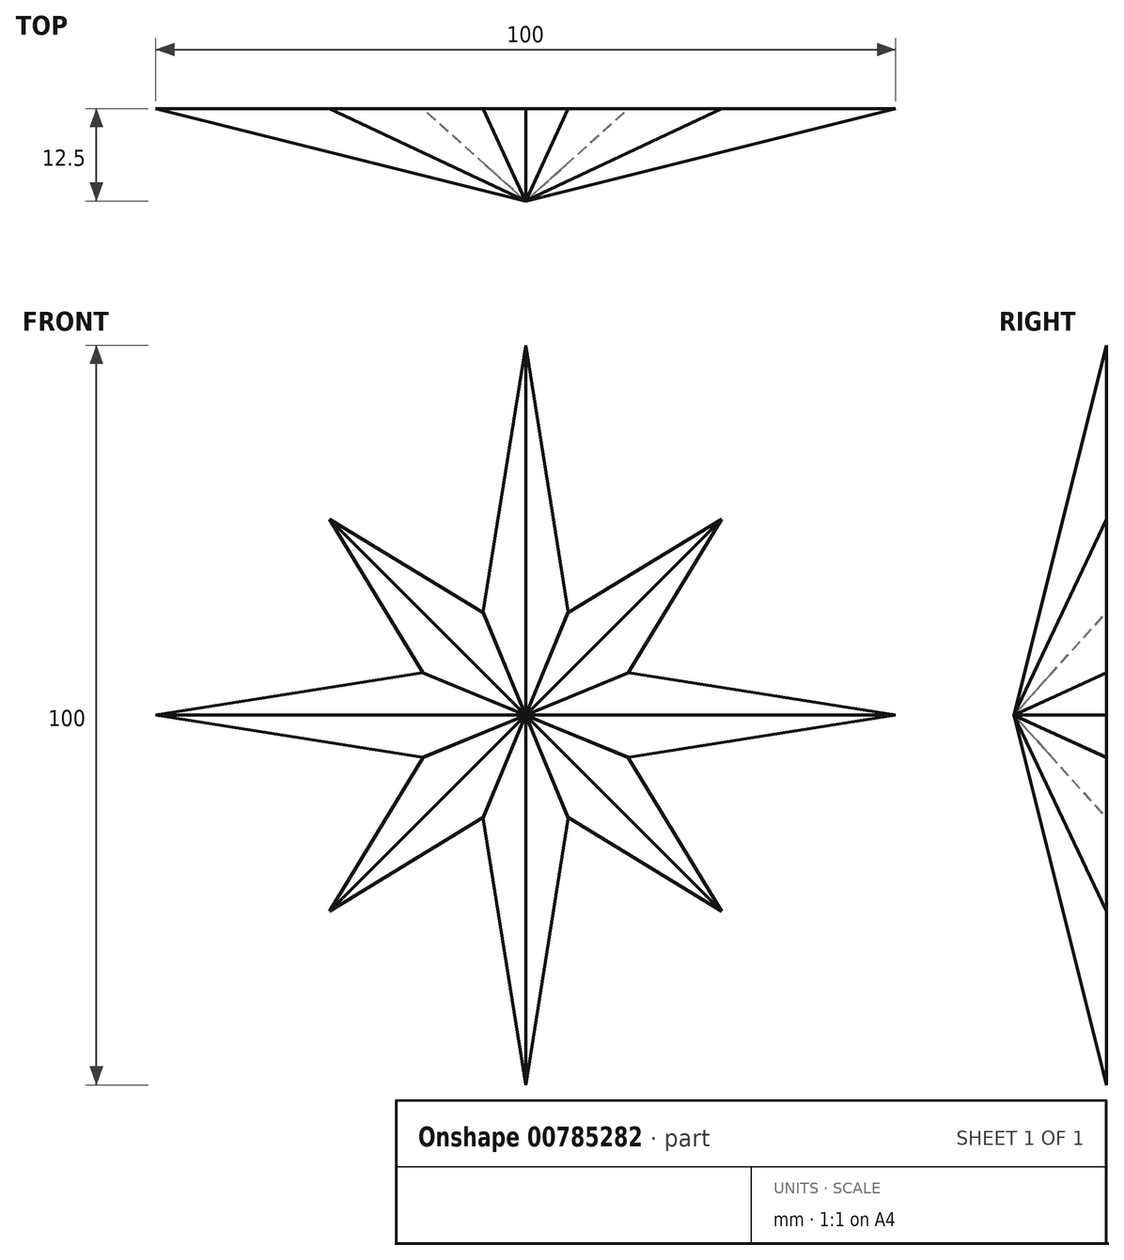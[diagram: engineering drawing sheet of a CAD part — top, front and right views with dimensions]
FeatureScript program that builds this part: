
annotation { "Feature Type Name" : "Feature", "Feature Type Description" : "" }
export const myFeature = defineFeature(function(context is Context, id is Id, definition is map)
    precondition{}
    {
        {
            var Q0;
            Q0=qCreatedBy(makeId("Front.planeOp"),FACE);
            var sketch = newSketch(context, id + "F0", { "sketchPlane" : qUnion([Q0])});
            skLineSegment(sketch, "E0", {"start": v(0, 0) * mm, "end": v(-50, 0) * mm});
            skLineSegment(sketch, "E1", {"start": v(0, 0) * mm, "end": v(-26.52, 26.52) * mm});
            skLineSegment(sketch, "E2", {"start": v(0, 0) * mm, "end": v(-13.86, 5.74) * mm});
            skPoint(sketch, "E3.center", {"position": v(0, 0) * mm});
            skLineSegment(sketch, "E4", {"start": v(-50, 0) * mm, "end": v(-13.86, 5.74) * mm});
            skLineSegment(sketch, "E5", {"start": v(-13.86, 5.74) * mm, "end": v(-26.52, 26.52) * mm});
            skSolve(sketch);
        }
        {
            var Q0;
            Q0=qCreatedBy(makeId("Right.planeOp"),FACE);
            var sketch = newSketch(context, id + "F1", { "sketchPlane" : qUnion([Q0])});
            skLineSegment(sketch, "E6", {"start": v(0, 0) * mm, "end": v(-12.5, 0) * mm});
            skSolve(sketch);
        }
        {
            var Q0;
            Q0=makeQuery(id+"F0.imprint","IMPRINT",FACE,{"disambiguationData":[TD([[makeQuery(id+"F0.imprint","IMPRINT",EDGE,{"derivedFrom":sQuery(id+"F0.wireOp",EDGE,"E0")}),-1.0]])]});
            var Q1;
            Q1=makeQuery(id+"F0.imprint","IMPRINT",FACE,{"disambiguationData":[TD([[makeQuery(id+"F0.imprint","IMPRINT",EDGE,{"derivedFrom":sQuery(id+"F0.wireOp",EDGE,"E1")}),1.0]])]});
            var Q2;
            Q2=sQuery(id+"F1.wireOp",VERTEX,"E6.end");
            extrude(context, id + "F2", {"entities" : qUnion([Q0, Q1]), "endBound" : BoundingType.UP_TO_VERTEX, "depth" : 25 * mm, "endBoundEntityVertex" : qUnion([Q2]), "offsetDistance" : 25 * mm});
        }
        {
            var Q0;
            Q0=sQuery(id+"F1.wireOp",VERTEX,"E6.end");
            var Q1;
            Q1=sQuery(id+"F0.wireOp",VERTEX,"E2.end");
            var Q2;
            Q2=sQuery(id+"F0.wireOp",VERTEX,"E0.end");
            cPlane(context, id + "F3", {"entities" : qUnion([Q0, Q1, Q2]), "cplaneType" : CPlaneType.THREE_POINT, "offset" : 25 * mm, "width" : 150 * mm, "height" : 150 * mm});
        }
        {
            var Q0;
            Q0=qCreatedBy(id+"F3.planeOp",FACE);
            var sketch = newSketch(context, id + "F4", { "sketchPlane" : qUnion([Q0])});
            skLineSegment(sketch, "E7", {"start": v(-53.08, -2.38) * mm, "end": v(-48.34, 21) * mm});
            skLineSegment(sketch, "E8", {"start": v(-48.34, 21) * mm, "end": v(0.9, 10.55) * mm});
            skLineSegment(sketch, "E9", {"start": v(0.9, 10.55) * mm, "end": v(-44.29, -33.47) * mm});
            skLineSegment(sketch, "E10", {"start": v(-44.29, -33.47) * mm, "end": v(-53.08, -2.38) * mm});
            skSolve(sketch);
        }
        {
            var Q0;
            Q0=makeQuery(id+"F4.imprint","IMPRINT",FACE,{"disambiguationData":[TD([[makeQuery(id+"F4.imprint","IMPRINT",EDGE,{"derivedFrom":sQuery(id+"F4.wireOp",EDGE,"E7")}),-1.0]])]});
            extrude(context, id + "F5", {"entities" : qUnion([Q0]), "depth" : -50 * mm, "offsetDistance" : 25 * mm});
        }
        {
            var Q0;
            Q0=makeQuery(id+"F5.opExtrude","SWEPT_BODY",BODY,{"disambiguationData":[OSD([sQuery(id+"F4.wireOp",EDGE,"E7"),sQuery(id+"F4.wireOp",EDGE,"E8"),sQuery(id+"F4.wireOp",EDGE,"E9"),sQuery(id+"F4.wireOp",EDGE,"E10")])]});
            var Q1;
            Q1=makeQuery(id+"F2.opExtrude","SWEPT_BODY",BODY,{"disambiguationData":[OSD([sQuery(id+"F0.wireOp",EDGE,"E0"),sQuery(id+"F0.wireOp",EDGE,"E1"),sQuery(id+"F0.wireOp",EDGE,"E4"),sQuery(id+"F0.wireOp",EDGE,"E5")])]});
            booleanBodies(context, id + "F6", {"operationType" : BooleanOperationType.SUBTRACTION, "tools" : qUnion([Q0]), "targets" : qUnion([Q1])});
        }
        {
            var Q0;
            Q0=sQuery(id+"F0.wireOp",VERTEX,"E2.end");
            var Q1;
            Q1=sQuery(id+"F1.wireOp",VERTEX,"E6.end");
            var Q2;
            Q2=sQuery(id+"F0.wireOp",VERTEX,"E1.end");
            cPlane(context, id + "F7", {"entities" : qUnion([Q0, Q1, Q2]), "cplaneType" : CPlaneType.THREE_POINT, "offset" : 25 * mm, "width" : 150 * mm, "height" : 150 * mm});
        }
        {
            var Q0;
            Q0=qCreatedBy(id+"F7.planeOp",FACE);
            var sketch = newSketch(context, id + "F8", { "sketchPlane" : qUnion([Q0])});
            skLineSegment(sketch, "E11", {"start": v(-10.2, 0) * mm, "end": v(5.37, 12.32) * mm});
            skLineSegment(sketch, "E12", {"start": v(5.37, 12.32) * mm, "end": v(8.1, 37.54) * mm});
            skLineSegment(sketch, "E13", {"start": v(8.1, 37.54) * mm, "end": v(-11, 36.94) * mm});
            skLineSegment(sketch, "E14", {"start": v(-11, 36.94) * mm, "end": v(-10.2, 0) * mm});
            skSolve(sketch);
        }
        {
            var Q0;
            Q0=makeQuery(id+"F8.imprint","IMPRINT",FACE,{"disambiguationData":[TD([[makeQuery(id+"F8.imprint","IMPRINT",EDGE,{"derivedFrom":sQuery(id+"F8.wireOp",EDGE,"E11")}),1.0]])]});
            extrude(context, id + "F9", {"entities" : qUnion([Q0]), "depth" : -50 * mm, "offsetDistance" : 25 * mm});
        }
        {
            var Q0;
            Q0=makeQuery(id+"F9.opExtrude","SWEPT_BODY",BODY,{"disambiguationData":[OSD([sQuery(id+"F8.wireOp",EDGE,"E11"),sQuery(id+"F8.wireOp",EDGE,"E12"),sQuery(id+"F8.wireOp",EDGE,"E13"),sQuery(id+"F8.wireOp",EDGE,"E14")])]});
            var Q1;
            Q1=makeQuery(id+"F2.opExtrude","SWEPT_BODY",BODY,{"disambiguationData":[OSD([sQuery(id+"F0.wireOp",EDGE,"E0"),sQuery(id+"F0.wireOp",EDGE,"E1"),sQuery(id+"F0.wireOp",EDGE,"E4"),sQuery(id+"F0.wireOp",EDGE,"E5")])]});
            booleanBodies(context, id + "F10", {"operationType" : BooleanOperationType.SUBTRACTION, "tools" : qUnion([Q0]), "targets" : qUnion([Q1])});
        }
        {
            var Q0;
            Q0=makeQuery(id+"F2.opExtrude","SWEPT_BODY",BODY,{"disambiguationData":[OSD([sQuery(id+"F0.wireOp",EDGE,"E0"),sQuery(id+"F0.wireOp",EDGE,"E1"),sQuery(id+"F0.wireOp",EDGE,"E4"),sQuery(id+"F0.wireOp",EDGE,"E5")])]});
            var Q1;
            Q1=makeQuery(id+"F2.opExtrude","SWEPT_FACE",FACE,{"disambiguationData":[OSD([sQuery(id+"F0.wireOp",EDGE,"E1")])]});
            mirror(context, id + "F11", {"operationType" : NewBodyOperationType.ADD, "entities" : qUnion([Q0]), "mirrorPlane" : qUnion([Q1])});
        }
        {
            var Q0;
            Q0=makeQuery(id+"F2.opExtrude","SWEPT_BODY",BODY,{"disambiguationData":[OSD([sQuery(id+"F0.wireOp",EDGE,"E0"),sQuery(id+"F0.wireOp",EDGE,"E1"),sQuery(id+"F0.wireOp",EDGE,"E4"),sQuery(id+"F0.wireOp",EDGE,"E5")])]});
            var Q1;
            Q1=sQuery(id+"F1.wireOp",EDGE,"E6");
            circularPattern(context, id + "F12", {"entities" : qUnion([Q0]), "axis" : qUnion([Q1]), "angle" : 360 * degree, "instanceCount" : 4, "equalSpace" : true});
        }
    });
